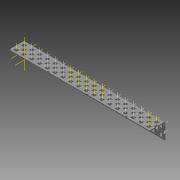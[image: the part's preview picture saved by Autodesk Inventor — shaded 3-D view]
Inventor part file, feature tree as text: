
AUTODESK INVENTOR PART (.ipt)
format: ipt  version: 2015 (Build 190159000, 159)  size: 2,119,680 bytes
history: native  units: in
note: dims shown in document units (in); Inventor stores cm internally (conversion verified against a paired STEP export)
features: other x113, pattern_linear x4, sheet_metal_op x1, extrude x1, imported_body x1, sketch x1
ambient origin geometry x8: Origin, YZ Plane, XZ Plane, XY Plane, X Axis, Y Axis, Z Axis, Center Point
bodies: Body1 (feature_tree)
feature tree (121):
  sheet_metal_op  "Fold1"
  other  "L-Channel"
  extrude  "length cut"  Depth=0.5in
  other  "top out axis"
  other  "top inner axis"
  other  "back out axis"
  other  "back inner axis"
  pattern_linear  "top outer axes"  Count1=2 Spacing1=0.5in
  pattern_linear  "top inner axes"  Spacing1=0.5in  [1 undecoded]
  pattern_linear  "back outer axes"  Count1=2 Spacing1=0.5in
  pattern_linear  "back inner axes"  Spacing1=0.5in  [1 undecoded]
  other  "right plane"
  imported_body  "Base1"
  sketch  "Sketch1"  dims[d1=0.0in d4=0.5in d5=0.7874in d7=0.5in d10=0.5in d13=0.5in d14=0.7874in d16=0.5in d19=0.5in d20=-9.0in d21=0.0in d22=0.0in d23=0.0in d24=0.0in d25=0.0in d26=0.0in]
  other  "Work Point1"
  other  "Work Point2"
  other  "Work Point3"
  other  "Work Point4"
  other  "Work Axis5"
  other  "Work Axis6"
  other  "Work Axis7"
  other  "Work Axis8"
  other  "Work Axis11"
  other  "Work Axis12"
  other  "Work Axis13"
  other  "Work Axis14"
  other  "Work Axis15"
  other  "Work Axis18"
  other  "Work Axis19"
  other  "Work Axis20"
  other  "Work Axis23"
  other  "Work Axis24"
  other  "Work Axis25"
  other  "Work Axis26"
  other  "Work Axis29"
  other  "Work Axis30"
  other  "Work Axis31"
  other  "Work Axis32"
  other  "Work Axis33"
  other  "Work Axis36"
  other  "Work Axis37"
  other  "Work Axis38"
  other  "Work Axis41"
  other  "Work Axis42"
  other  "Work Axis43"
  other  "Work Axis44"
  other  "Work Axis45"
  other  "Work Axis46"
  other  "Work Axis47"
  other  "Work Axis48"
  other  "Work Axis49"
  other  "Work Axis50"
  other  "Work Axis51"
  other  "Work Axis52"
  other  "Work Axis53"
  other  "Work Axis61"
  other  "Work Axis62"
  other  "Work Axis63"
  other  "Work Axis64"
  other  "Work Axis65"
  other  "Work Axis66"
  other  "Work Axis67"
  other  "Work Axis68"
  other  "Work Axis69"
  other  "Work Axis70"
  other  "Work Axis71"
  other  "Work Axis72"
  other  "Work Axis73"
  other  "Work Axis81"
  other  "Work Axis82"
  other  "Work Axis83"
  other  "Work Axis84"
  other  "Work Axis85"
  other  "Work Axis86"
  other  "Work Axis87"
  other  "Work Axis88"
  other  "Work Axis89"
  other  "Work Axis90"
  other  "Work Axis91"
  other  "Work Axis92"
  other  "Work Axis93"
  other  "Work Axis101"
  other  "Work Axis102"
  other  "Work Axis103"
  other  "Work Axis104"
  other  "Work Axis105"
  other  "Work Axis106"
  other  "Work Axis107"
  other  "Work Axis108"
  other  "Work Axis109"
  other  "Work Axis110"
  other  "Work Axis111"
  other  "Work Axis112"
  other  "Work Axis113"
  other  "Work Axis121"
  other  "Work Axis122"
  other  "Work Axis123"
  other  "Work Axis124"
  other  "Work Axis125"
  other  "Work Axis126"
  other  "Work Axis127"
  other  "Work Axis128"
  other  "Work Axis129"
  other  "Work Axis130"
  other  "Work Axis131"
  other  "Work Axis132"
  other  "Work Axis133"
  other  "Work Axis141"
  other  "Work Axis142"
  other  "Work Axis143"
  other  "Work Axis144"
  other  "Work Axis145"
  other  "Work Axis146"
  other  "Work Axis147"
  other  "Work Axis148"
  other  "Work Axis149"
  other  "Work Axis150"
  other  "Work Axis151"
  other  "Work Axis152"
  other  "Work Axis153"
  other  "left plane"
note: 2 required parameter values undecoded (feature->parameter linkage not recoverable at this tier; creation-order binding heuristic only, values carry confidence <= 0.55)
